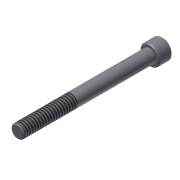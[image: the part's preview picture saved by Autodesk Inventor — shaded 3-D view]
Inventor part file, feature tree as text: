
AUTODESK INVENTOR PART (.ipt)
format: ipt  version: 2013 (Build 170138000, 138)  size: 100,352 bytes
history: native  units: in
note: dims shown in document units (in); Inventor stores cm internally (conversion verified against a paired STEP export)
features: extrude x3, sketch x3, chamfer x1, thread x1
ambient origin geometry x8: Origin, YZ Plane, XZ Plane, XY Plane, X Axis, Y Axis, Z Axis, Center Point
bodies: Solid1 (feature_tree)
feature tree (8):
  extrude  "Extrusion1"  Depth=2.5in TaperAngle=0.0deg
  extrude  "Extrusion2"  Depth=0.25in TaperAngle=0.0deg
  extrude  "Extrusion3"  Depth=0.125in TaperAngle=0.0deg
  chamfer  "Chamfer1"  Distance=0.02in Angle=45.0deg
  thread  "Thread1"  [1 undecoded]
  sketch  "Sketch1"  dims[d0=0.25in d1=2.5in d2=0.0in]
  sketch  "Sketch2"  dims[d3=0.375in d4=0.25in d5=0.0in]
  sketch  "Sketch3"  dims[d6=0.1875in d7=0.125in d8=0.0in d9=0.02in d10=0.125in d11=45.0deg d12=1.0in d13=0.0in]
note: 1 required parameter value undecoded (feature->parameter linkage not recoverable at this tier; creation-order binding heuristic only, values carry confidence <= 0.55)
